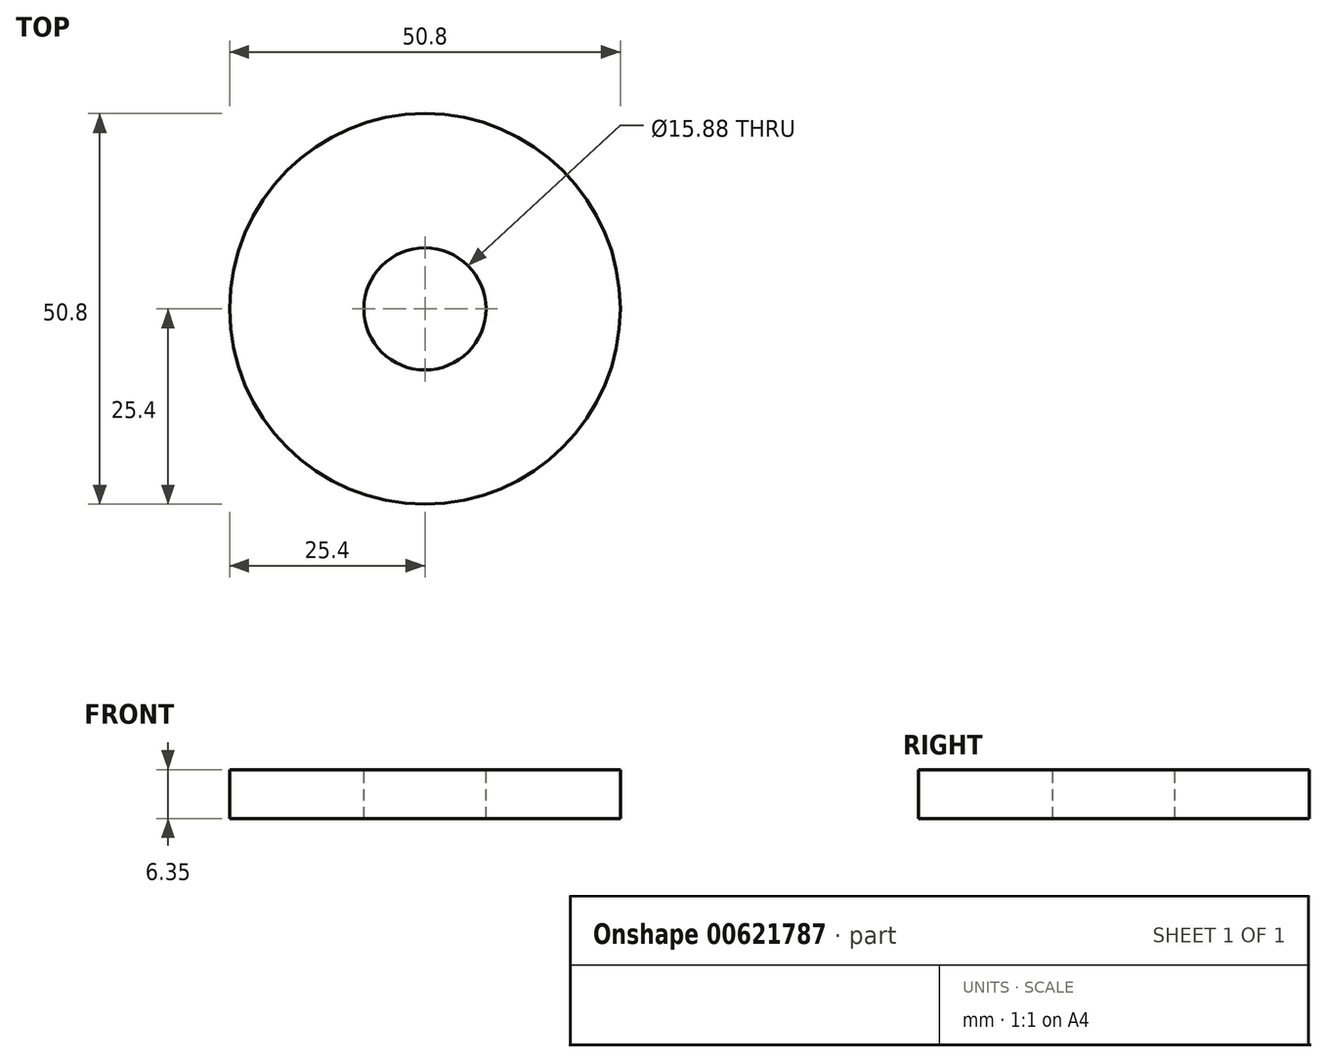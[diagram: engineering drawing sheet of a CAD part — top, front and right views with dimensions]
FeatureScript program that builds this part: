
annotation { "Feature Type Name" : "Feature", "Feature Type Description" : "" }
export const myFeature = defineFeature(function(context is Context, id is Id, definition is map)
    precondition{}
    {
        {
            var Q0;
            Q0=qCreatedBy(makeId("Top.planeOp"),FACE);
            var sketch = newSketch(context, id + "F0", { "sketchPlane" : qUnion([Q0])});
            skCircle(sketch, "E0", {"center": v(0, 0) * mm, "radius": 25.4 * mm});
            skCircle(sketch, "E1", {"center": v(0, 0) * mm, "radius": 7.94 * mm});
            skSolve(sketch);
        }
        {
            var Q0;
            Q0=makeQuery(id+"F0.imprint","IMPRINT",FACE,{"disambiguationData":[TD([[makeQuery(id+"F0.imprint","IMPRINT",EDGE,{"derivedFrom":sQuery(id+"F0.wireOp",EDGE,"E0")}),1.0]])]});
            extrude(context, id + "F1", {"entities" : qUnion([Q0]), "oppositeDirection" : true, "depth" : 6.35 * mm, "offsetDistance" : 25.4 * mm});
        }
    });
